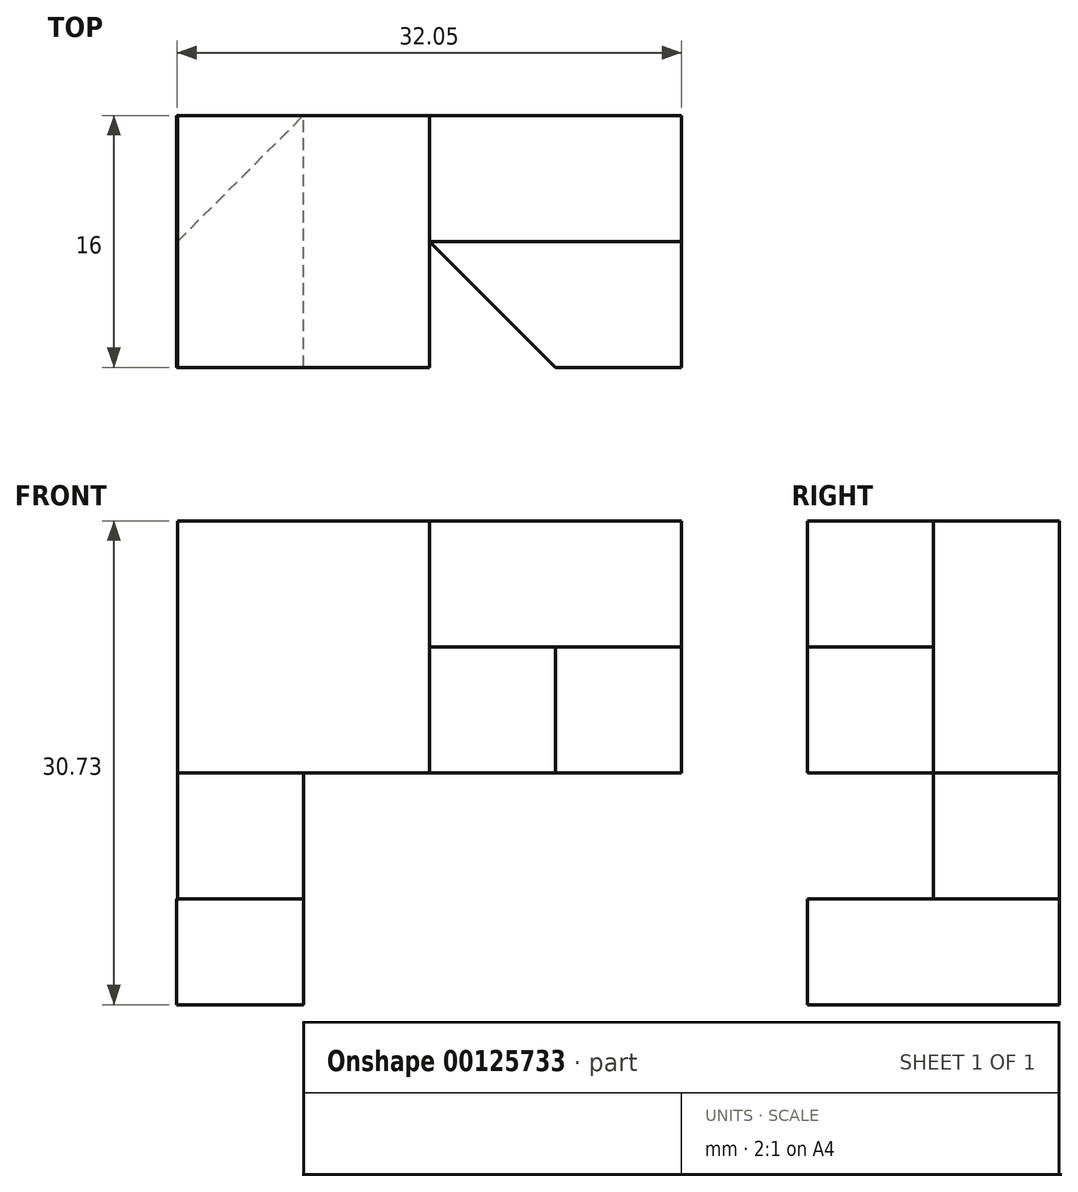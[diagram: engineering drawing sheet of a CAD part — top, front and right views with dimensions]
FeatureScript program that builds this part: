
annotation { "Feature Type Name" : "Feature", "Feature Type Description" : "" }
export const myFeature = defineFeature(function(context is Context, id is Id, definition is map)
    precondition{}
    {
        {
            var Q0;
            Q0=qCreatedBy(makeId("Front.planeOp"),FACE);
            var sketch = newSketch(context, id + "F0", { "sketchPlane" : qUnion([Q0])});
            skLineSegment(sketch, "E0.bottom", {"start": v(-57.6, 50.62) * mm, "end": v(-41.6, 50.62) * mm});
            skLineSegment(sketch, "E0.top", {"start": v(-57.6, 34.62) * mm, "end": v(-41.6, 34.62) * mm});
            skLineSegment(sketch, "E0.left", {"start": v(-57.6, 50.62) * mm, "end": v(-57.6, 34.62) * mm});
            skLineSegment(sketch, "E0.right", {"start": v(-41.6, 50.62) * mm, "end": v(-41.6, 34.62) * mm});
            skPoint(sketch, "E1.oppositeSnap0", {"position": v(-49.6, 34.62) * mm});
            skLineSegment(sketch, "E1.bottom", {"start": v(-41.6, 50.62) * mm, "end": v(-25.6, 50.62) * mm});
            skLineSegment(sketch, "E1.top", {"start": v(-41.6, 34.62) * mm, "end": v(-25.6, 34.62) * mm});
            skLineSegment(sketch, "E1.right", {"start": v(-25.6, 50.62) * mm, "end": v(-25.6, 34.62) * mm});
            skSolve(sketch);
        }
        {
            var Q0;
            Q0=makeQuery(id+"F0.imprint","IMPRINT",FACE,{"disambiguationData":[TD([[makeQuery(id+"F0.imprint","IMPRINT",EDGE,{"derivedFrom":sQuery(id+"F0.wireOp",EDGE,"E1.bottom")}),-1.0]])]});
            extrude(context, id + "F1", {"entities" : qUnion([Q0]), "depth" : 8 * mm});
        }
        {
            var Q0;
            Q0=makeQuery(id+"F0.imprint","IMPRINT",FACE,{"disambiguationData":[TD([[makeQuery(id+"F0.imprint","IMPRINT",EDGE,{"derivedFrom":sQuery(id+"F0.wireOp",EDGE,"E0.bottom")}),-1.0]])]});
            extrude(context, id + "F2", {"entities" : qUnion([Q0]), "depth" : 16 * mm});
        }
        {
            var Q0;
            Q0=makeQuery(id+"F1.opExtrude","CAP_FACE",FACE,{"disambiguationData":[OSD([sQuery(id+"F0.wireOp",EDGE,"E1.bottom"),sQuery(id+"F0.wireOp",EDGE,"E1.top"),sQuery(id+"F0.wireOp",EDGE,"E0.right"),sQuery(id+"F0.wireOp",EDGE,"E1.right")])],"isStart":false});
            var sketch = newSketch(context, id + "F3", { "sketchPlane" : qUnion([Q0])});
            skLineSegment(sketch, "E2.bottom", {"start": v(-41.6, 42.62) * mm, "end": v(-25.6, 42.62) * mm});
            skLineSegment(sketch, "E2.top", {"start": v(-41.6, 34.62) * mm, "end": v(-25.6, 34.62) * mm});
            skLineSegment(sketch, "E2.left", {"start": v(-41.6, 42.62) * mm, "end": v(-41.6, 34.62) * mm});
            skLineSegment(sketch, "E2.right", {"start": v(-25.6, 42.62) * mm, "end": v(-25.6, 34.62) * mm});
            skSolve(sketch);
        }
        {
            var Q0;
            Q0=makeQuery(id+"F3.imprint","IMPRINT",FACE,{"disambiguationData":[TD([[makeQuery(id+"F3.imprint","IMPRINT",EDGE,{"derivedFrom":sQuery(id+"F3.wireOp",EDGE,"E2.bottom")}),-1.0]])]});
            extrude(context, id + "F4", {"entities" : qUnion([Q0]), "depth" : 8 * mm});
        }
        {
            var Q0;
            Q0=makeQuery(id+"F4.opExtrude","SWEPT_FACE",FACE,{"disambiguationData":[OSD([sQuery(id+"F3.wireOp",EDGE,"E2.top")])]});
            var sketch = newSketch(context, id + "F5", { "sketchPlane" : qUnion([Q0])});
            skLineSegment(sketch, "E3", {"start": v(-33.6, 16) * mm, "end": v(-41.6, 8) * mm});
            skSolve(sketch);
        }
        {
            var Q0;
            {var subQ0=sQuery(id+"F5.wireOp",EDGE,"E3");Q0=makeQuery(id+"F5.imprint","IMPRINT",FACE,{"disambiguationData":[TD([[makeQuery(id+"F5.imprint","IMPRINT",EDGE,{"derivedFrom":subQ0}),-1.0]])]});}
            extrude(context, id + "F6", {"entities" : qUnion([Q0]), "operationType" : NewBodyOperationType.REMOVE, "oppositeDirection" : true, "depth" : 8 * mm});
        }
        {
            var Q0;
            Q0=makeQuery(id+"F2.opExtrude","SWEPT_FACE",FACE,{"disambiguationData":[OSD([sQuery(id+"F0.wireOp",EDGE,"E0.top")])]});
            var sketch = newSketch(context, id + "F7", { "sketchPlane" : qUnion([Q0])});
            skLineSegment(sketch, "E4", {"start": v(-57.6, 8) * mm, "end": v(-49.6, 0) * mm});
            skSolve(sketch);
        }
        {
            var Q0;
            {var subQ0=sQuery(id+"F7.wireOp",EDGE,"E4");Q0=makeQuery(id+"F7.imprint","IMPRINT",FACE,{"disambiguationData":[TD([[makeQuery(id+"F7.imprint","IMPRINT",EDGE,{"derivedFrom":subQ0}),-1.0]])]});}
            extrude(context, id + "F8", {"entities" : qUnion([Q0]), "operationType" : NewBodyOperationType.ADD, "depth" : 8 * mm});
        }
        {
            var Q0;
            Q0=qCreatedBy(makeId("Front.planeOp"),FACE);
            var sketch = newSketch(context, id + "F9", { "sketchPlane" : qUnion([Q0])});
            skLineSegment(sketch, "E5.bottom", {"start": v(-57.65, 26.6) * mm, "end": v(-49.6, 26.6) * mm});
            skLineSegment(sketch, "E5.top", {"start": v(-57.65, 19.9) * mm, "end": v(-49.6, 19.9) * mm});
            skLineSegment(sketch, "E5.left", {"start": v(-57.65, 26.6) * mm, "end": v(-57.65, 19.9) * mm});
            skLineSegment(sketch, "E5.right", {"start": v(-49.6, 26.6) * mm, "end": v(-49.6, 19.9) * mm});
            skSolve(sketch);
        }
        {
            var Q0;
            Q0=makeQuery(id+"F9.imprint","IMPRINT",FACE,{"disambiguationData":[TD([[makeQuery(id+"F9.imprint","IMPRINT",EDGE,{"derivedFrom":sQuery(id+"F9.wireOp",EDGE,"E5.bottom")}),-1.0]])]});
            extrude(context, id + "F10", {"entities" : qUnion([Q0]), "depth" : 16 * mm});
        }
    });
